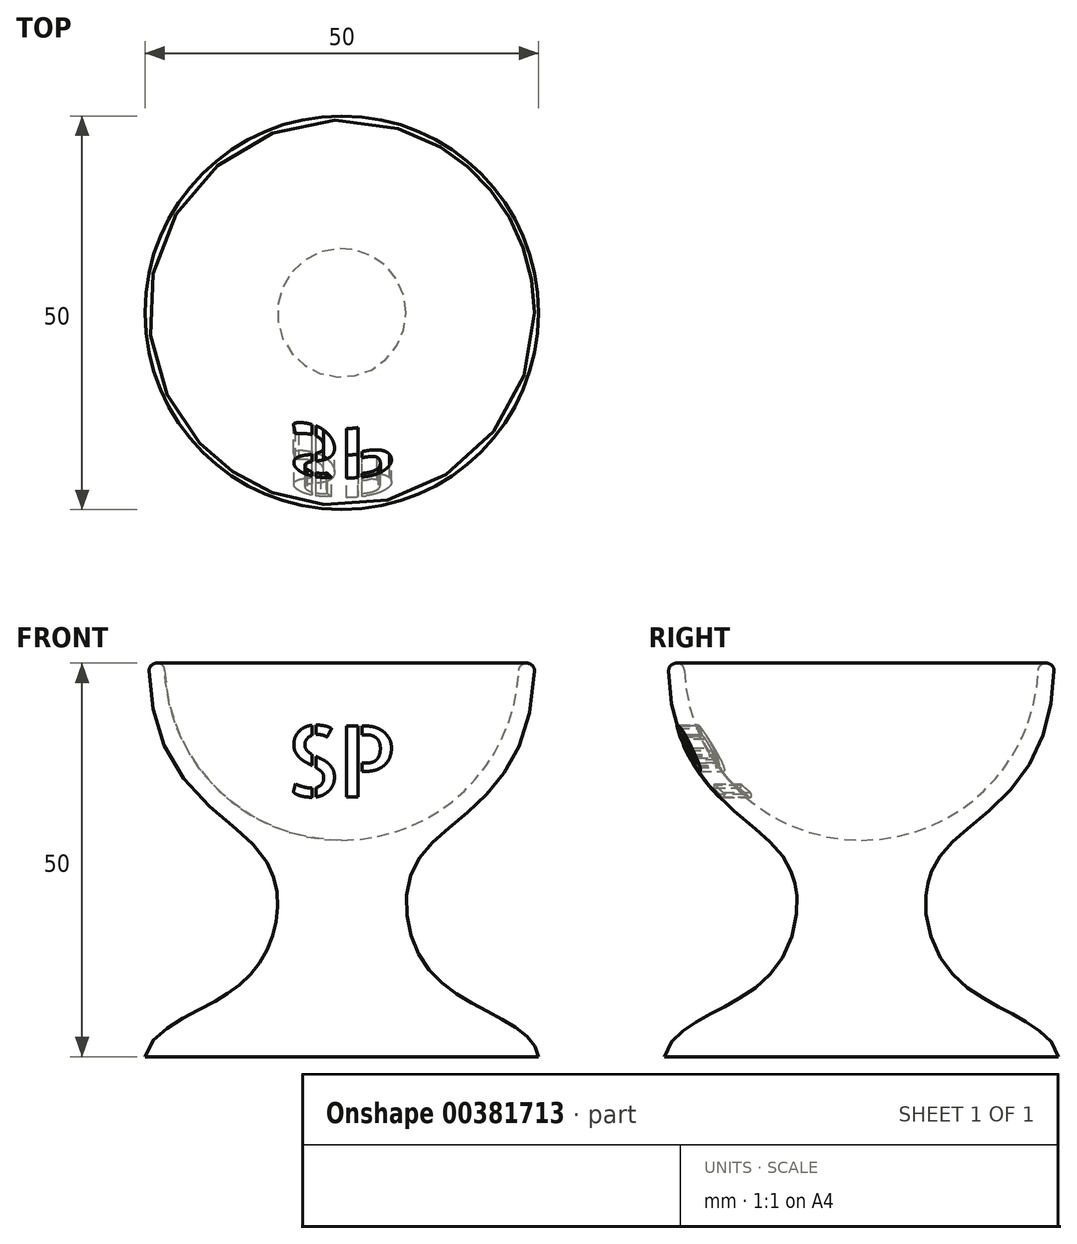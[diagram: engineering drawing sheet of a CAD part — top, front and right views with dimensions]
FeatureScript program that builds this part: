
annotation { "Feature Type Name" : "Feature", "Feature Type Description" : "" }
export const myFeature = defineFeature(function(context is Context, id is Id, definition is map)
    precondition{}
    {
        {
            var Q0;
            Q0=qCreatedBy(makeId("Front.planeOp"),FACE);
            var sketch = newSketch(context, id + "F0", { "sketchPlane" : qUnion([Q0])});
            skCircle(sketch, "E0", {"center": v(0, 50) * mm, "radius": 22.5 * mm});
            skLineSegment(sketch, "E1", {"start": v(0, 50) * mm, "end": v(0, 0) * mm});
            skFitSpline(sketch, "E2", {"points": [v(24.5, 50) * mm, v(9.62, 24.91) * mm, v(10.77, 11.44) * mm, v(20.54, 4.66) * mm, v(25, 0) * mm], "startDerivative": vector(-0.43, -141.75) * mm, "endDerivative": vector(4.3, -31.99) * mm});
            skLineSegment(sketch, "E3", {"start": v(24.5, 50) * mm, "end": v(0, 50) * mm});
            skLineSegment(sketch, "E4", {"start": v(25, 0) * mm, "end": v(0, 0) * mm});
            skSolve(sketch);
        }
        {
            var Q0;
            {var subQ1=sQuery(id+"F0.wireOp",EDGE,"E2");Q0=makeQuery(id+"F0.imprint","IMPRINT",FACE,{"disambiguationData":[TD([[makeQuery(id+"F0.imprint","IMPRINT",EDGE,{"derivedFrom":subQ1}),-1.0]])]});}
            var Q1;
            Q1=sQuery(id+"F0.wireOp",EDGE,"E1");
            revolve(context, id + "F1", {"entities" : qUnion([Q0]), "axis" : qUnion([Q1]), "revolveType" : RevolveType.FULL});
        }
        {
            var Q0;
            Q0=makeQuery(id+"F1.opRevolve","SWEPT_EDGE",EDGE,{"disambiguationData":[OSD([sQuery(id+"F0.wireOp",EDGE,"E2"),sQuery(id+"F0.wireOp",EDGE,"E3")])]});
            var Q1;
            Q1=makeQuery(id+"F1.opRevolve","SWEPT_EDGE",EDGE,{"disambiguationData":[OSD([sQuery(id+"F0.wireOp",EDGE,"E0"),sQuery(id+"F0.wireOp",EDGE,"E3")])]});
            fillet(context, id + "F2", {"entities" : qUnion([Q0, Q1]), "radius" : 1 * mm, "tangentPropagation" : true, "allowEdgeOverflow" : false});
        }
        {
            var Q0;
            Q0=qCreatedBy(makeId("Front.planeOp"),FACE);
            var sketch = newSketch(context, id + "F3", { "sketchPlane" : qUnion([Q0])});
            skText(sketch, "E5", { "text": "SP", "fontName": "AllertaStencil-Regular.ttf"});
            skLineSegment(sketch, "E6", {"start": v(0, 33) * mm, "end": v(0, 0) * mm, "construction": true});
            const initialGuessF3  = {"E5": [-0.00714, 0.033, 1, 0, 0.009]};
            skSetInitialGuess(sketch, initialGuessF3);
            skSolve(sketch);
        }
        {
            var Q0;
            Q0=qSketchRegion(id+"F3",true);
            extrude(context, id + "F4", {"entities" : qUnion([Q0]), "operationType" : NewBodyOperationType.REMOVE, "depth" : 25 * mm});
        }
    });
